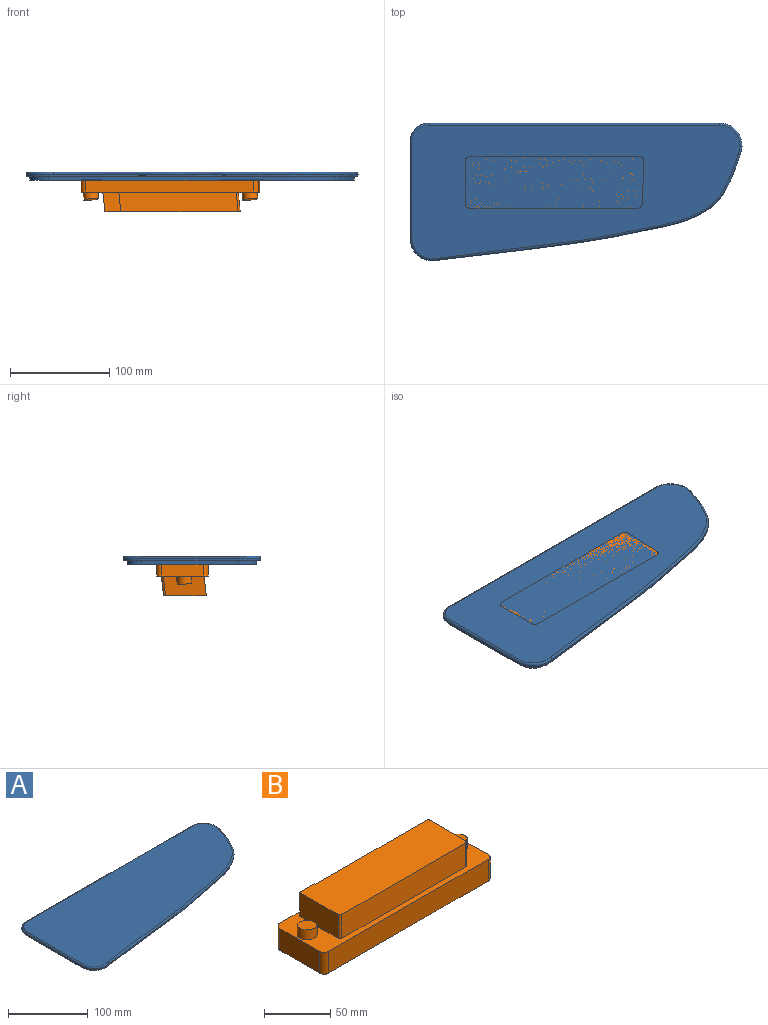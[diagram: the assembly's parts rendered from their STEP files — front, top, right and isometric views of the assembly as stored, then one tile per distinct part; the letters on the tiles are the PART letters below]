
ASSEMBLY  parts=2 mates=1
PART A: 21 faces, bbox 337.4x142.4x8 mm
  f0: cylinder r=14.35mm len=14.35mm, axis (0,0,1), area 90.1mm2, adj f1,f5,f6,f7
  f1: plane 292.89x4mm, normal (0,1,0), area 1171.6mm2, adj f0,f2,f6,f7
  f2: cylinder r=18.5mm len=18.5mm, axis (0,0,1), area 115.8mm2, adj f1,f3,f6,f7
  f3: extruded ~307.35x111.89mm, area 1407mm2, adj f2,f4,f6,f7
  f4: cylinder r=18.5mm len=18.5mm, axis (0,0,1), area 115.8mm2, adj f3,f5,f6,f7
  f5: plane 97.44x4mm, normal (-1,0,0), area 389.8mm2, adj f0,f4,f6,f7
  f6: plane 325.74x130.29mm, normal (0,0,-1), area 34675.8mm2, adj f0,f1,f2,f3,f4,f5
  f7: plane 333.74x138.29mm, normal (0,0,-1), area 3341.5mm2, adj f0,f1,f2,f3,f4,f5,f8,f9
  f8: cylinder r=18.35mm len=18.35mm, axis (0,0,-1), area 57.6mm2, adj f7,f9,f13,f17
  f9: plane 292.89x2mm, normal (0,1,0), area 585.8mm2, adj f7,f8,f10,f15
  f10: cylinder r=22.5mm len=31.55mm, axis (0,0,-1), area 89.3mm2, adj f7,f9,f11,f16
  f11: extruded ~304.36x106.18mm, area 686.9mm2, adj f7,f10,f12,f18
  f12: cylinder r=22.5mm len=27.48mm, axis (0,0,-1), area 80.7mm2, adj f7,f11,f13,f20
  f13: plane 97.44x2mm, normal (-1,0,0), area 194.9mm2, adj f7,f8,f12,f19
  f14: plane 329.74x134.29mm, normal (0,0,1), area 36336.6mm2, adj f15,f16,f17,f18,f19,f20
  f15: cylinder r=2mm len=292.89mm, axis (-1,0,0), area 920.1mm2, adj f9,f14,f16,f17
  f16: torus R=20.5mm, axis (0,0,-1), area 136mm2, adj f10,f14,f15,f18
  f17: torus R=16.35mm, axis (0,0,-1), area 87mm2, adj f8,f14,f15,f19
  f18: bspline ~329.46x110mm, area 1076.7mm2, adj f11,f14,f16,f20
  f19: cylinder r=2mm len=97.44mm, axis (0,-1,0), area 306.1mm2, adj f13,f14,f17,f20
  f20: torus R=20.5mm, axis (0,0,-1), area 122.9mm2, adj f12,f14,f18,f19
PART B: 24 faces, bbox 179.9x52.1x40.1 mm
  f0: plane 14.86x14.86mm, normal (0.1,0.1,0.99), area 175mm2, adj f1
  f1: bspline ~15.77x15.71mm, area 352.3mm2, adj f0,f23
  f2: plane 136.06x43.06mm, normal (0,0,1), area 5725.4mm2, adj f3,f4,f5,f6,f7,f8,f9,f10
  f3: plane 20x18mm, normal (0,1,-0.1), area 321.6mm2, adj f2,f4,f11,f23
  f4: plane 20x3mm, normal (1,0,-0.1), area 20.1mm2, adj f2,f3,f5,f23
  f5: plane 120x20mm, normal (0,1,-0.1), area 2371.8mm2, adj f2,f4,f6,f23
  f6: bspline ~20x4mm, area 63.3mm2, adj f2,f5,f7,f23
  f7: plane 40x20mm, normal (1,0,-0.1), area 763.8mm2, adj f2,f6,f8,f23
  f8: bspline ~20x4mm, area 62.9mm2, adj f2,f7,f9,f23
  f9: plane 134x20mm, normal (0,-1,0.1), area 2653.2mm2, adj f2,f8,f10,f23
  f10: bspline ~20x4mm, area 63.3mm2, adj f2,f9,f11,f23
  f11: plane 43x20mm, normal (-1,0,0.1), area 824.1mm2, adj f2,f3,f10,f23
  f12: plane 14.86x14.86mm, normal (0.1,0.1,0.99), area 175mm2, adj f13
  f13: bspline ~15.77x15.71mm, area 352.3mm2, adj f12,f23
  f14: plane 42x20mm, normal (1,0.04,0), area 840.6mm2, adj f15,f21,f22,f23
  f15: cylinder r=5mm len=20mm, axis (0,0,1), area 160.9mm2, adj f14,f16,f22,f23
  f16: plane 169.8x20mm, normal (0,-1,0), area 3396.1mm2, adj f15,f17,f22,f23
  f17: cylinder r=5mm len=20mm, axis (0,0,1), area 157.1mm2, adj f16,f18,f22,f23
  f18: plane 42x20mm, normal (-1,0,0), area 840mm2, adj f17,f19,f22,f23
  f19: cylinder r=5mm len=20mm, axis (0,0,1), area 157.1mm2, adj f18,f20,f22,f23
  f20: plane 168.19x20mm, normal (0,1,0), area 3363.8mm2, adj f19,f21,f22,f23
  f21: cylinder r=5mm len=20mm, axis (0,0,1), area 153.2mm2, adj f14,f20,f22,f23
  f22: plane 179.8x52mm, normal (0,0,-1), area 9286.5mm2, adj f14,f15,f16,f17,f18,f19,f20,f21
  f23: plane 179.87x52.06mm, normal (0,0,1), area 3207.6mm2, adj f1,f3,f4,f5,f6,f7,f8,f9
PLACE A t=(-26.88,-14.98,-0.06)mm
PLACE B rot(axis=(1,0,0),180deg) t=(-37.02,199.4,-19.06)mm
MATE fastened B.f22 <-> A.f14  axis (0,0,1) through (-37.52,-0.55,0.94)mm
